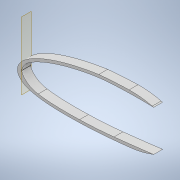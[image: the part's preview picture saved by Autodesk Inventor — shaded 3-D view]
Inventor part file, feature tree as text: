
AUTODESK INVENTOR PART (.ipt)
format: ipt  version: 2022.1 (Build 261234020, 234B)  size: 587,776 bytes
history: native  units: mm
features: sketch x7, extrude x6, thicken_offset x4, fillet x3, projected_geometry x3, shell x1, plane x1, other x1
ambient origin geometry x8: Origin, YZ Plane, XZ Plane, XY Plane, X Axis, Y Axis, Z Axis, Center Point
bodies: Solid1 (feature_tree)
feature tree (26):
  extrude  "Extrusion1"  Depth=10.0mm
  shell  "Shell1"  Thickness=1.0mm
  thicken_offset  "Thicken1"
  extrude  "Extrusion27"  TaperAngle=0.0deg  [1 undecoded]
  thicken_offset  "Thicken3"
  extrude  "Extrusion29"  Depth=20.0mm
  plane  "Work Plane5"
  other  "Bend Part2"
  thicken_offset  "Thicken5"
  extrude  "Extrusion30"  Depth=10.0mm TaperAngle=0.0deg
  extrude  "Extrusion31"  Depth=100.0mm
  fillet  "Fillet6"  Radius=1.0mm
  fillet  "Fillet7"  Radius=100.0mm
  thicken_offset  "Thicken6"
  extrude  "Extrusion32"  Depth=10.0mm TaperAngle=0.0deg
  fillet  "Fillet8"  Radius=150.0mm
  sketch  "Sketch3"  dims[d0=10.0mm d1=0.0mm d2=3.0mm d159=1.0mm d160=2.0mm]
  sketch  "Sketch48"  dims[d236=190.0mm d237=0.0mm d238=0.0mm]
  sketch  "Sketch55"  dims[d249=2.0mm d250=1.0mm d254=20.0mm]
  projected_geometry  "Projected Loop32"
  sketch  "Sketch57"  dims[d255=8.0mm d256=10.0mm d257=0.0mm]
  sketch  "Sketch58"  dims[d262=10.0mm d263=0.349066mm d264=1.0mm d265=1.0mm d268=100.0mm]
  projected_geometry  "Projected Loop34"
  sketch  "Sketch59"  dims[d269=5.0mm d270=10.0mm d271=0.0mm d272=150.0mm]
  sketch  "Sketch60"  dims[d273=100.0mm d274=0.0mm d275=550.0mm d276=100.0mm d277=6.0mm d278=2000.0mm d279=500.0mm d280=200.0mm d281=2.0mm d282=2.0mm d283=3.0mm d284=450.0mm d285=3.0mm d287=800.0mm d288=10.0mm d289=0.0mm d290=100.0mm]
  projected_geometry  "Projected Loop35"
note: 1 required parameter value undecoded (feature->parameter linkage not recoverable at this tier; creation-order binding heuristic only, values carry confidence <= 0.55)
